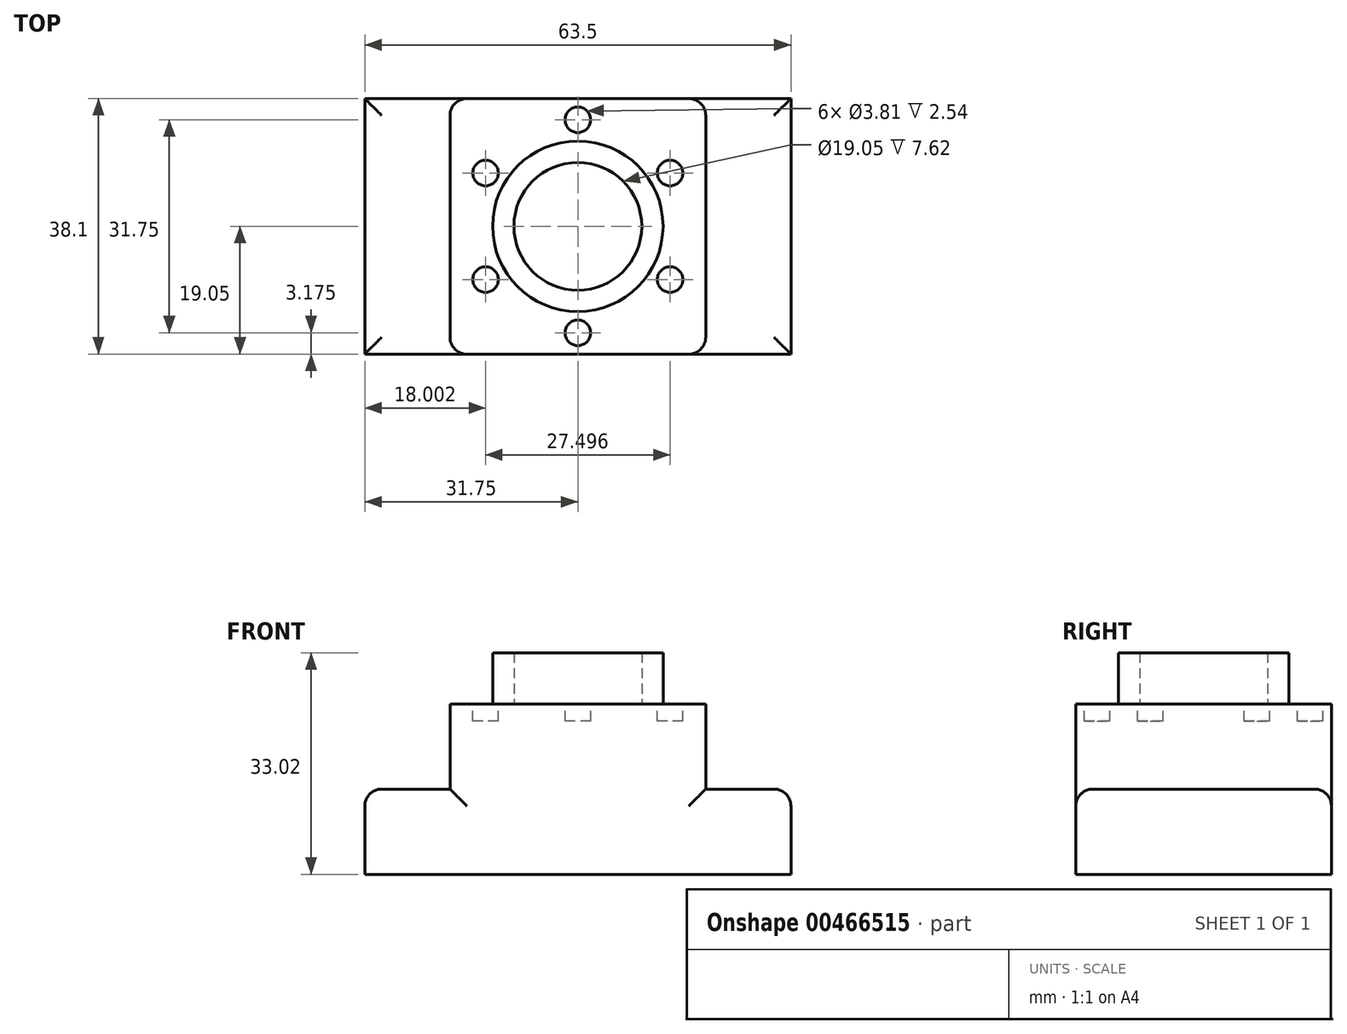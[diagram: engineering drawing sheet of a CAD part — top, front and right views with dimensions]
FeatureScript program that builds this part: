
annotation { "Feature Type Name" : "Feature", "Feature Type Description" : "" }
export const myFeature = defineFeature(function(context is Context, id is Id, definition is map)
    precondition{}
    {
        {
            var Q0;
            Q0=qCreatedBy(makeId("Front.planeOp"),FACE);
            var sketch = newSketch(context, id + "F0", { "sketchPlane" : qUnion([Q0])});
            skLineSegment(sketch, "E0.bottom", {"start": v(-31.75, 6.35) * mm, "end": v(31.75, 6.35) * mm});
            skLineSegment(sketch, "E0.top", {"start": v(-31.75, -6.35) * mm, "end": v(31.75, -6.35) * mm});
            skLineSegment(sketch, "E0.left", {"start": v(-31.75, 6.35) * mm, "end": v(-31.75, -6.35) * mm});
            skLineSegment(sketch, "E0.right", {"start": v(31.75, 6.35) * mm, "end": v(31.75, -6.35) * mm});
            skPoint(sketch, "E0.middle", {"position": v(0, 0) * mm});
            skLineSegment(sketch, "E1.bottom", {"start": v(19.05, 6.35) * mm, "end": v(-19.05, 6.35) * mm});
            skLineSegment(sketch, "E1.top", {"start": v(19.05, 19.05) * mm, "end": v(-19.05, 19.05) * mm});
            skLineSegment(sketch, "E1.left", {"start": v(19.05, 6.35) * mm, "end": v(19.05, 19.05) * mm});
            skLineSegment(sketch, "E1.right", {"start": v(-19.05, 6.35) * mm, "end": v(-19.05, 19.05) * mm});
            skSolve(sketch);
        }
        {
            var Q0;
            Q0 = qSketchRegion(id + "F0", true);
            extrude(context, id + "F1", {"entities" : qUnion([Q0]), "endBound" : BoundingType.SYMMETRIC, "depth" : 38.1 * mm});
        }
        {
            var Q0;
            Q0=makeQuery(id+"F1.opExtrude","SWEPT_FACE",FACE,{"disambiguationData":[OSD([sQuery(id+"F0.wireOp",EDGE,"E1.top")])]});
            var sketch = newSketch(context, id + "F2", { "sketchPlane" : qUnion([Q0])});
            skCircle(sketch, "E2", {"center": v(0, 0) * mm, "radius": 12.7 * mm});
            skCircle(sketch, "E3", {"center": v(0, 0) * mm, "radius": 9.53 * mm});
            skSolve(sketch);
        }
        {
            var Q0;
            Q0 = qSketchRegion(id + "F2", true);
            extrude(context, id + "F3", {"entities" : qUnion([Q0]), "operationType" : NewBodyOperationType.ADD, "depth" : 7.62 * mm});
        }
        {
            var Q0;
            {var subQ1=sQuery(id+"F0.wireOp",EDGE,"E1.left");var subQ2=sQuery(id+"F0.wireOp",EDGE,"E1.top");Q0=makeQuery(id+"F3.boolean.opBoolean","SPLIT",FACE,{"disambiguationData":[TD([makeQuery(id+"F1.opExtrude","SWEPT_FACE",FACE,{"disambiguationData":[OSD([subQ1])]})])],"derivedFrom":makeQuery(id+"F1.opExtrude","SWEPT_FACE",FACE,{"disambiguationData":[OSD([subQ2])]})});}
            var sketch = newSketch(context, id + "F4", { "sketchPlane" : qUnion([Q0])});
            skCircle(sketch, "E4", {"center": v(0, 0) * mm, "radius": 15.88 * mm, "construction": true});
            skCircle(sketch, "E5", {"center": v(0, 15.88) * mm, "radius": 1.9 * mm});
            skPoint(sketch, "E6", {"position": v(0, 19.05) * mm});
            skCircle(sketch, "E7.1.0", {"center": v(13.75, 7.94) * mm, "radius": 1.9 * mm});
            skCircle(sketch, "E7.2.0", {"center": v(13.75, -7.94) * mm, "radius": 1.9 * mm});
            skCircle(sketch, "E7.3.0", {"center": v(0, -15.88) * mm, "radius": 1.9 * mm});
            skCircle(sketch, "E7.4.0", {"center": v(-13.75, -7.94) * mm, "radius": 1.9 * mm});
            skCircle(sketch, "E7.5.0", {"center": v(-13.75, 7.94) * mm, "radius": 1.9 * mm});
            skLineSegment(sketch, "E7.anchor1", {"start": v(0, 0) * mm, "end": v(0, 15.88) * mm, "construction": true});
            skLineSegment(sketch, "E7.anchor2", {"start": v(0, 0) * mm, "end": v(-13.75, 7.94) * mm, "construction": true});
            skSolve(sketch);
        }
        {
            var Q0;
            Q0=makeQuery(id+"F4.imprint","IMPRINT",FACE,{"disambiguationData":[TD([[makeQuery(id+"F4.imprint","IMPRINT",EDGE,{"derivedFrom":sQuery(id+"F4.wireOp",EDGE,"E7.2.0")}),1.0]])]});
            var Q1;
            Q1=makeQuery(id+"F4.imprint","IMPRINT",FACE,{"disambiguationData":[TD([[makeQuery(id+"F4.imprint","IMPRINT",EDGE,{"derivedFrom":sQuery(id+"F4.wireOp",EDGE,"E7.1.0")}),1.0]])]});
            var Q2;
            Q2=makeQuery(id+"F4.imprint","IMPRINT",FACE,{"disambiguationData":[TD([[makeQuery(id+"F4.imprint","IMPRINT",EDGE,{"derivedFrom":sQuery(id+"F4.wireOp",EDGE,"E5")}),1.0]])]});
            var Q3;
            Q3=makeQuery(id+"F4.imprint","IMPRINT",FACE,{"disambiguationData":[TD([[makeQuery(id+"F4.imprint","IMPRINT",EDGE,{"derivedFrom":sQuery(id+"F4.wireOp",EDGE,"E7.5.0")}),1.0]])]});
            var Q4;
            Q4=makeQuery(id+"F4.imprint","IMPRINT",FACE,{"disambiguationData":[TD([[makeQuery(id+"F4.imprint","IMPRINT",EDGE,{"derivedFrom":sQuery(id+"F4.wireOp",EDGE,"E7.4.0")}),1.0]])]});
            var Q5;
            Q5=makeQuery(id+"F4.imprint","IMPRINT",FACE,{"disambiguationData":[TD([[makeQuery(id+"F4.imprint","IMPRINT",EDGE,{"derivedFrom":sQuery(id+"F4.wireOp",EDGE,"E7.3.0")}),1.0]])]});
            extrude(context, id + "F5", {"entities" : qUnion([Q0, Q1, Q2, Q3, Q4, Q5]), "operationType" : NewBodyOperationType.REMOVE, "oppositeDirection" : true, "depth" : 2.54 * mm});
        }
        {
            var Q0;
            {var subQ0=sQuery(id+"F0.wireOp",EDGE,"E0.bottom");Q0=makeQuery(id+"F1.opExtrude","CAP_EDGE",EDGE,{"disambiguationData":[OSD([subQ0]),TDD([makeQuery(id+"F0.imprint","IMPRINT",EDGE,{"disambiguationData":[TD([[makeQuery(id+"F0.imprint","INTERSECT",VERTEX,{"derivedFrom":[subQ0,sQuery(id+"F0.wireOp",EDGE,"E0.right")]}),1.0]])],"derivedFrom":subQ0})])],"isStart":true});}
            var Q1;
            Q1=makeQuery(id+"F1.opExtrude","SWEPT_EDGE",EDGE,{"disambiguationData":[OSD([sQuery(id+"F0.wireOp",EDGE,"E0.bottom"),sQuery(id+"F0.wireOp",EDGE,"E0.right")])]});
            var Q2;
            {var subQ0=sQuery(id+"F0.wireOp",EDGE,"E0.bottom");Q2=makeQuery(id+"F1.opExtrude","CAP_EDGE",EDGE,{"disambiguationData":[OSD([subQ0]),TDD([makeQuery(id+"F0.imprint","IMPRINT",EDGE,{"disambiguationData":[TD([[makeQuery(id+"F0.imprint","INTERSECT",VERTEX,{"derivedFrom":[subQ0,sQuery(id+"F0.wireOp",EDGE,"E0.right")]}),1.0]])],"derivedFrom":subQ0})])],"isStart":false});}
            var Q3;
            Q3=makeQuery(id+"F1.opExtrude","CAP_EDGE",EDGE,{"disambiguationData":[OSD([sQuery(id+"F0.wireOp",EDGE,"E1.right")])],"isStart":true});
            var Q4;
            {var subQ0=sQuery(id+"F0.wireOp",EDGE,"E0.bottom");Q4=makeQuery(id+"F1.opExtrude","CAP_EDGE",EDGE,{"disambiguationData":[OSD([subQ0]),TDD([makeQuery(id+"F0.imprint","IMPRINT",EDGE,{"disambiguationData":[TD([[makeQuery(id+"F0.imprint","INTERSECT",VERTEX,{"derivedFrom":[subQ0,sQuery(id+"F0.wireOp",EDGE,"E0.left")]}),-1.0]])],"derivedFrom":subQ0})])],"isStart":true});}
            var Q5;
            Q5=makeQuery(id+"F1.opExtrude","SWEPT_EDGE",EDGE,{"disambiguationData":[OSD([sQuery(id+"F0.wireOp",EDGE,"E0.bottom"),sQuery(id+"F0.wireOp",EDGE,"E0.left")])]});
            var Q6;
            {var subQ0=sQuery(id+"F0.wireOp",EDGE,"E0.bottom");Q6=makeQuery(id+"F1.opExtrude","CAP_EDGE",EDGE,{"disambiguationData":[OSD([subQ0]),TDD([makeQuery(id+"F0.imprint","IMPRINT",EDGE,{"disambiguationData":[TD([[makeQuery(id+"F0.imprint","INTERSECT",VERTEX,{"derivedFrom":[subQ0,sQuery(id+"F0.wireOp",EDGE,"E0.left")]}),-1.0]])],"derivedFrom":subQ0})])],"isStart":false});}
            var Q7;
            Q7=makeQuery(id+"F1.opExtrude","CAP_EDGE",EDGE,{"disambiguationData":[OSD([sQuery(id+"F0.wireOp",EDGE,"E1.right")])],"isStart":false});
            var Q8;
            Q8=makeQuery(id+"F1.opExtrude","CAP_EDGE",EDGE,{"disambiguationData":[OSD([sQuery(id+"F0.wireOp",EDGE,"E1.left")])],"isStart":false});
            var Q9;
            Q9=makeQuery(id+"F1.opExtrude","CAP_EDGE",EDGE,{"disambiguationData":[OSD([sQuery(id+"F0.wireOp",EDGE,"E1.left")])],"isStart":true});
            fillet(context, id + "F6", {"entities" : qUnion([Q0, Q1, Q2, Q3, Q4, Q5, Q6, Q7, Q8, Q9]), "radius" : 2.54 * mm, "tangentPropagation" : true, "allowEdgeOverflow" : false});
        }
    });
